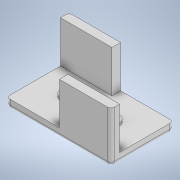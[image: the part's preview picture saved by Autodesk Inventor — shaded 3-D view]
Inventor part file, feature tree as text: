
AUTODESK INVENTOR PART (.ipt)
format: ipt  version: 2022 (Build 260153000, 153)  size: 172,544 bytes
history: native  units: in
note: dims shown in document units (in); Inventor stores cm internally (conversion verified against a paired STEP export)
features: extrude x5, sketch x5, chamfer x1, fillet x1
ambient origin geometry x8: Origin, YZ Plane, XZ Plane, XY Plane, X Axis, Y Axis, Z Axis, Center Point
bodies: Solid1 (feature_tree)
feature tree (12):
  extrude  "Extrusion1"  Depth=1.4331in
  extrude  "Extrusion2"  Depth=1.1811in
  extrude  "Extrusion3"  Depth=1.1811in
  extrude  "Extrusion4"  Depth=0.9606in TaperAngle=0.0deg
  extrude  "Extrusion5"  Depth=0.0787in
  chamfer  "Chamfer1"  Distance=0.1181in
  fillet  "Fillet1"  Radius=0.1575in
  sketch  "Sketch1"  dims[d0=2.3937in d1=1.4331in]
  sketch  "Sketch2"  dims[d2=0.1969in d3=0.0in d4=1.1811in]
  sketch  "Sketch3"  dims[d5=0.1969in d6=1.1811in]
  sketch  "Sketch4"  dims[d7=0.1969in d8=0.9606in d9=0.0in]
  sketch  "Sketch5"  dims[d10=0.3406in d11=0.3406in d12=0.1181in d13=0.0in d14=0.1575in d15=0.1575in d16=0.5906in d17=0.0in d18=0.2362in d19=0.2362in d20=0.1181in d21=0.0in d22=0.0591in d23=0.0787in d24=45.0deg d25=0.0787in]
